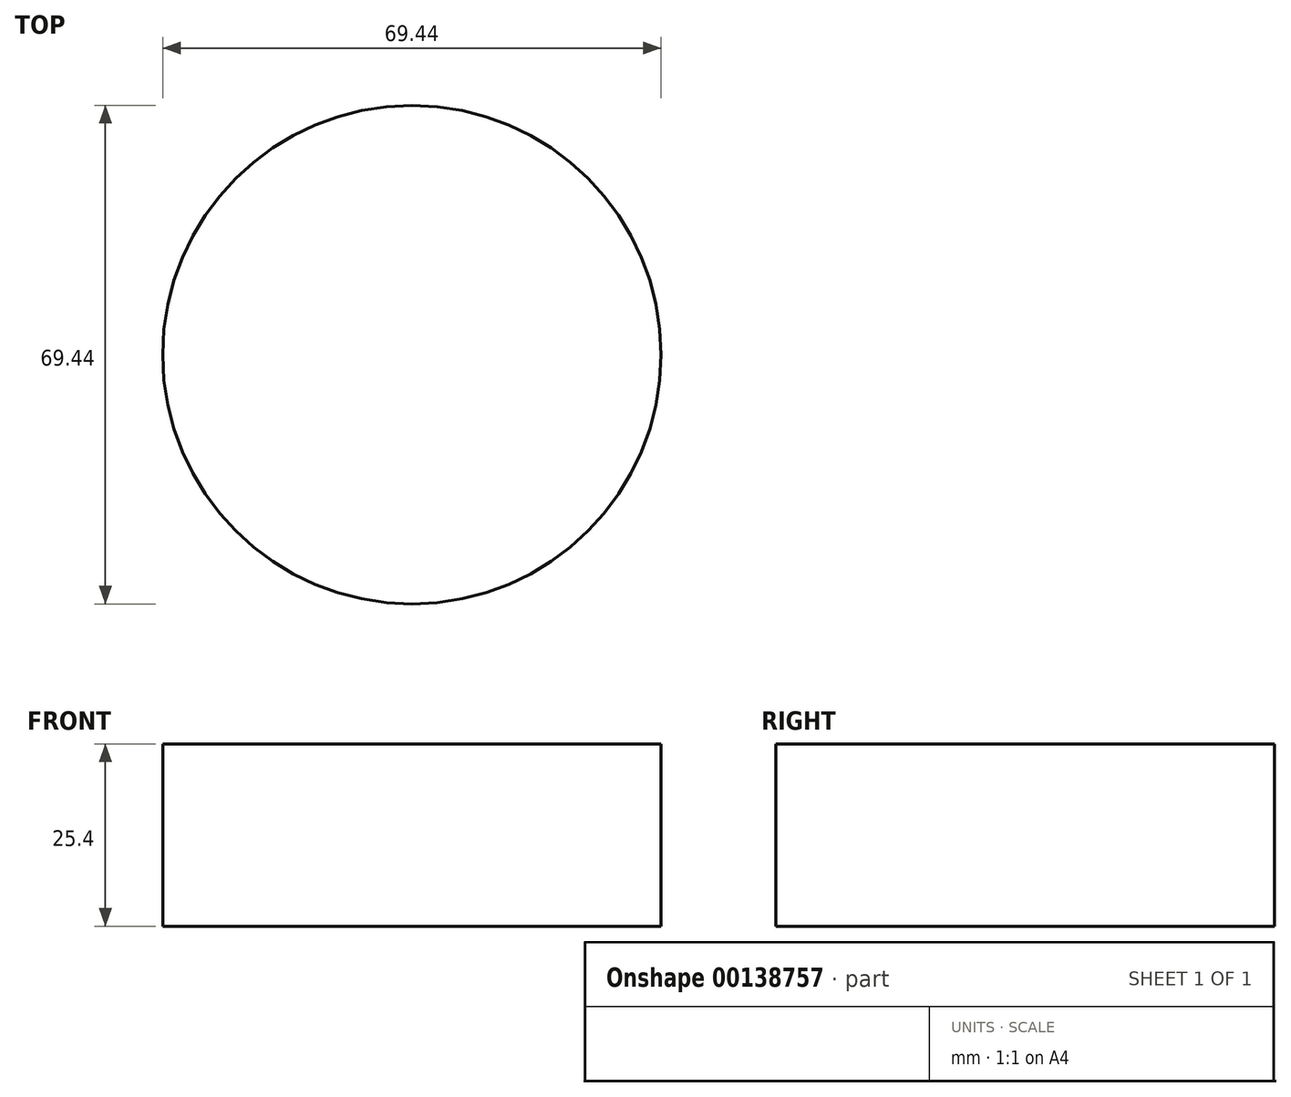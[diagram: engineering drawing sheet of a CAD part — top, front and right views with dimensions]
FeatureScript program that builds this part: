
annotation { "Feature Type Name" : "Feature", "Feature Type Description" : "" }
export const myFeature = defineFeature(function(context is Context, id is Id, definition is map)
    precondition{}
    {
        {
            var Q0;
            Q0=qCreatedBy(makeId("Top.planeOp"),FACE);
            var sketch = newSketch(context, id + "F0", { "sketchPlane" : qUnion([Q0])});
            skCircle(sketch, "E0", {"center": v(0, 0) * mm, "radius": 34.72 * mm});
            skSolve(sketch);
        }
        {
            var Q0;
            Q0 = qSketchRegion(id + "F0", true);
            extrude(context, id + "F1", {"entities" : qUnion([Q0]), "depth" : 25.4 * mm});
        }
    });
